# Revit family: Tub_Spout-American_Standard-Aspirations-8888116_Series
name_source: partatom
category: Plumbing Fixtures
units: mm (PartAtom-declared; Revit-internal decimal feet)

## family parameters
Cut with Voids When Loaded = No
Host = Face
OmniClass Number = 23.45.05.14.21
OmniClass Title = Bathtubs
Part Type = Normal
Room Calculation Point = No
Round Connector Dimension = Use Diameter
Shared = Yes

## types (3) — shared parameters
ADA Compliant = Yes
ANSI A117.1 = Yes
ASME A112.18.1/CSA B125.1 = Yes
Assembly Code = D2020300
CEC Compliant = Yes
CW Connection = No
CWFU = 3
Connection Description = 1" IPS/Slip-On Supply Inlet
Default Elevation = 21"
Description = Aspirations™ Waterfall Tub Spout
Diameter = 3 1/2"
HW Connection = No
HWFU = 3
Height = 2"
Installation Type = Wall Mounted
Length = 4 9/16"
Manufacturer = American Standard
Tempered Water Connection = Yes
URL = https://www.americanstandard-us.com
Vent Connection = No
WFU = 4
Waste Connection = No
Water Connection Diameter = 1"
Width = 10"

## per-type parameters (varying)
| type | Finish | Material |
| 8888116.002 | Metal-American Standard-002-Polished Chrome | Metal-American Standard-002-Polished Chrome |
| 8888116.295 | Metal-American Standard-295-Brushed Nickel | Metal-American Standard-295-Brushed Nickel |
| 8888116.243 | Metal-American Standard-243-Matte Black | Metal-American Standard-243-Matte Black |

note: column(s) folded — value = type name in every type: Model

## geometry (parser evidence)
native form markers: Sweep x3
no freeform markers — native parametric forms only
